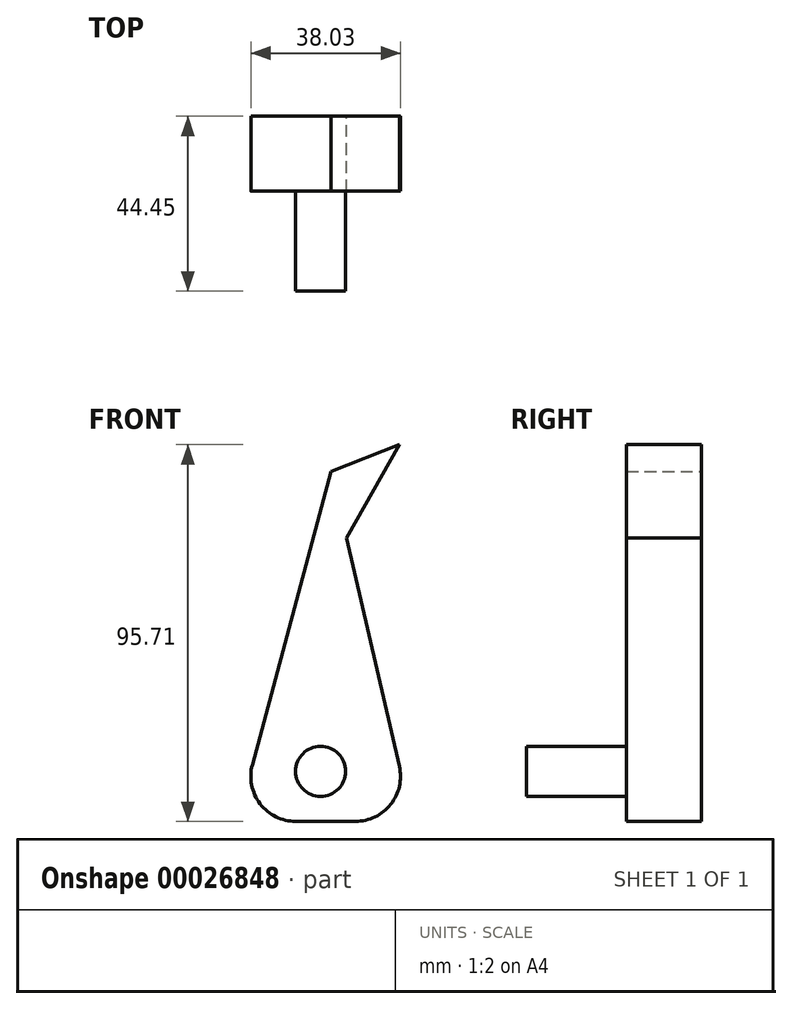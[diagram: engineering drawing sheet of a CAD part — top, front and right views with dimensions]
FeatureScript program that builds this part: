
annotation { "Feature Type Name" : "Feature", "Feature Type Description" : "" }
export const myFeature = defineFeature(function(context is Context, id is Id, definition is map)
    precondition{}
    {
        {
            var Q0;
            Q0=qCreatedBy(makeId("Front.planeOp"),FACE);
            var sketch = newSketch(context, id + "F0", { "sketchPlane" : qUnion([Q0])});
            skLineSegment(sketch, "E0.bottom", {"start": v(-1.47, -45.31) * mm, "end": v(13.7, -45.31) * mm});
            skLineSegment(sketch, "E1", {"start": v(7.46, 43.59) * mm, "end": v(-12.5, -30.92) * mm});
            skLineSegment(sketch, "E2", {"start": v(11.37, 26.74) * mm, "end": v(24.83, -31.3) * mm});
            skPoint(sketch, "E0.left.end.orphan", {"position": v(-14.73, 42.26) * mm});
            skPoint(sketch, "E0.right.end.orphan", {"position": v(29.64, 44.92) * mm});
            skLineSegment(sketch, "E3", {"start": v(7.46, 43.59) * mm, "end": v(24.93, 50.4) * mm});
            skLineSegment(sketch, "E4", {"start": v(24.93, 50.4) * mm, "end": v(11.37, 26.74) * mm});
            skPoint(sketch, "E5.orphan", {"position": v(-4.45, -0.86) * mm});
            skCircle(sketch, "E6", {"center": v(4.84, -32.61) * mm, "radius": 6.35 * mm});
            skPoint(sketch, "E7.visualSharp", {"position": v(-16.36, -45.31) * mm});
            skArc(sketch, "E7.filletArc", {"start": v(-12.5, -30.92) * mm, "mid": v(-10.54, -40.84) * mm, "end": v(-1.47, -45.31) * mm});
            skPoint(sketch, "E8.visualSharp", {"position": v(28.09, -45.31) * mm});
            skArc(sketch, "E8.filletArc", {"start": v(13.7, -45.31) * mm, "mid": v(22.65, -41) * mm, "end": v(24.83, -31.3) * mm});
            skSolve(sketch);
        }
        {
            var Q0;
            Q0=makeQuery(id+"F0.imprint","IMPRINT",FACE,{"disambiguationData":[TD([[makeQuery(id+"F0.imprint","IMPRINT",EDGE,{"derivedFrom":sQuery(id+"F0.wireOp",EDGE,"E0.bottom")}),1.0]])]});
            extrude(context, id + "F1", {"entities" : qUnion([Q0]), "depth" : 19.05 * mm});
        }
        {
            var Q0;
            Q0=makeQuery(id+"F0.imprint","IMPRINT",FACE,{"disambiguationData":[TD([[makeQuery(id+"F0.imprint","IMPRINT",EDGE,{"derivedFrom":sQuery(id+"F0.wireOp",EDGE,"E6")}),1.0]])]});
            extrude(context, id + "F2", {"entities" : qUnion([Q0]), "operationType" : NewBodyOperationType.ADD, "depth" : 44.45 * mm});
        }
    });
